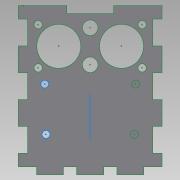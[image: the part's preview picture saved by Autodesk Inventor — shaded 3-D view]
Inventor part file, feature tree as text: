
AUTODESK INVENTOR PART (.ipt)
format: ipt  version: 2015 SP1 (Build 190203100, 203)  size: 248,320 bytes
history: native  units: mm
features: extrude x4, sketch x3, projected_geometry x1
ambient origin geometry x8: Origin, YZ Plane, XZ Plane, XY Plane, X Axis, Y Axis, Z Axis, Center Point
bodies: Body1 (feature_tree)
feature tree (8):
  extrude  "Extrusion2"  Depth=3.0mm
  extrude  "Extrusion3"  Depth=3.0mm
  sketch  "Sketch3"  dims[d14=180.0deg d15=3.0mm d17=7.675mm d18=7.675mm d21=3.0mm d22=0.0mm d23=2.999814mm d24=0.5mm d25=0.5mm d26=3.0mm d27=0.0mm d28=0.5mm d29=0.5mm d30=11.700171mm d31=11.699829mm d32=7.675mm d33=7.675mm d34=11.699829mm d35=11.700171mm d45=8.061mm d46=8.061mm d47=10.0mm d48=0.0mm d49=3.0mm d50=0.0mm]
  extrude  "Extrusion4"  Depth=3.0mm
  extrude  "Extrusion5"  Depth=3.0mm
  sketch  "Sketch1"  dims[d0=10.0mm d1=3.0mm]
  sketch  "Sketch2"  dims[d2=20.0mm d4=15.0mm d5=20.0mm d7=15.0mm d13=3.0mm]
  projected_geometry  "Projected Loop1"
